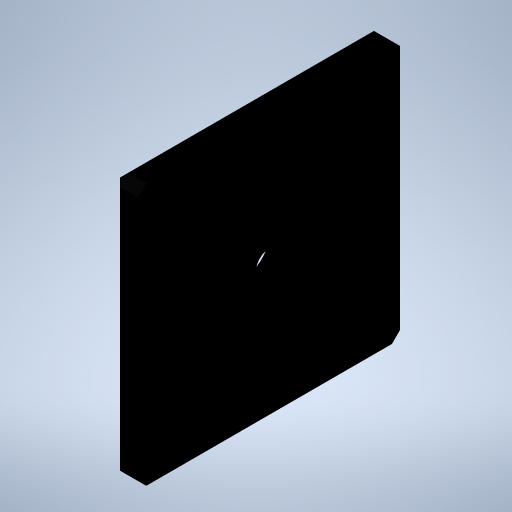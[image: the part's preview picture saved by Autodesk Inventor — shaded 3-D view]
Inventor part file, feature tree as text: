
AUTODESK INVENTOR PART (.ipt)
format: ipt  version: 2023 (Build 270158000, 158)  size: 263,680 bytes
history: native  units: mm
features: other x98, sketch x2, extrude x1, hole x1, chamfer x1
ambient origin geometry x8: Origin, YZ Plane, XZ Plane, XY Plane, X Axis, Y Axis, Z Axis, Center Point
bodies: Solid1 (feature_tree)
feature tree (103):
  extrude  "Extrusion1"  TaperAngle=0.0deg  [1 undecoded]
  hole  "Hole1"  [1 undecoded]
  other  "CS_ANBAU_CAP_XY"
  other  "CS_ANBAU_CAP_YZ"
  other  "CS_ANBAU_CAP_ZX"
  other  "CS_ANBAU_CAP_X"
  other  "CS_ANBAU_CAP_Y"
  other  "CS_ANBAU_CAP_Z"
  other  "CS_ANBAU_CAP_Center"
  other  "CS_ANBAU_CAP_90_XY"
  other  "CS_ANBAU_CAP_90_YZ"
  other  "CS_ANBAU_CAP_90_ZX"
  other  "CS_ANBAU_CAP_90_X"
  other  "CS_ANBAU_CAP_90_Y"
  other  "CS_ANBAU_CAP_90_Z"
  other  "CS_ANBAU_CAP_90_Center"
  other  "IB_1_XY"
  other  "IB_1_YZ"
  other  "IB_1_ZX"
  other  "IB_1_X"
  other  "IB_1_Y"
  other  "IB_1_Z"
  other  "IB_1_Center"
  other  "IB_10_XY"
  other  "IB_10_YZ"
  other  "IB_10_ZX"
  other  "IB_10_X"
  other  "IB_10_Y"
  other  "IB_10_Z"
  other  "IB_10_Center"
  other  "IB_11_XY"
  other  "IB_11_YZ"
  other  "IB_11_ZX"
  other  "IB_11_X"
  other  "IB_11_Y"
  other  "IB_11_Z"
  other  "IB_11_Center"
  other  "IB_12_XY"
  other  "IB_12_YZ"
  other  "IB_12_ZX"
  other  "IB_12_X"
  other  "IB_12_Y"
  other  "IB_12_Z"
  other  "IB_12_Center"
  other  "IB_2_XY"
  other  "IB_2_YZ"
  other  "IB_2_ZX"
  other  "IB_2_X"
  other  "IB_2_Y"
  other  "IB_2_Z"
  other  "IB_2_Center"
  other  "IB_3_XY"
  other  "IB_3_YZ"
  other  "IB_3_ZX"
  other  "IB_3_X"
  other  "IB_3_Y"
  other  "IB_3_Z"
  other  "IB_3_Center"
  other  "IB_4_XY"
  other  "IB_4_YZ"
  other  "IB_4_ZX"
  other  "IB_4_X"
  other  "IB_4_Y"
  other  "IB_4_Z"
  other  "IB_4_Center"
  other  "IB_5_XY"
  other  "IB_5_YZ"
  other  "IB_5_ZX"
  other  "IB_5_X"
  other  "IB_5_Y"
  other  "IB_5_Z"
  other  "IB_5_Center"
  other  "IB_6_XY"
  other  "IB_6_YZ"
  other  "IB_6_ZX"
  other  "IB_6_X"
  other  "IB_6_Y"
  other  "IB_6_Z"
  other  "IB_6_Center"
  other  "IB_7_XY"
  other  "IB_7_YZ"
  other  "IB_7_ZX"
  other  "IB_7_X"
  other  "IB_7_Y"
  other  "IB_7_Z"
  other  "IB_7_Center"
  other  "IB_8_XY"
  other  "IB_8_YZ"
  other  "IB_8_ZX"
  other  "IB_8_X"
  other  "IB_8_Y"
  other  "IB_8_Z"
  other  "IB_8_Center"
  other  "IB_9_XY"
  other  "IB_9_YZ"
  other  "IB_9_ZX"
  other  "IB_9_X"
  other  "IB_9_Y"
  other  "IB_9_Z"
  other  "IB_9_Center"
  chamfer  "Chamfer1"  [1 undecoded]
  sketch  "Skizze_1"  dims[d0=4.0mm d1=0.0mm]
  sketch  "Sketch2"  dims[d2=4.0mm d3=6.0mm d4=8.1mm d5=2.0mm d6=90.0deg d7=4.0mm d8=0.0mm d9=0.0mm d10=0.0mm d11=0.0mm d12=0.0mm d13=0.0mm d14=0.0mm d15=0.0mm d16=0.0mm d17=0.0mm d18=0.0mm d19=0.0mm d20=0.0mm d21=1.25mm d22=2.0mm d23=45.0deg]
note: 3 required parameter values undecoded (feature->parameter linkage not recoverable at this tier; creation-order binding heuristic only, values carry confidence <= 0.55)
